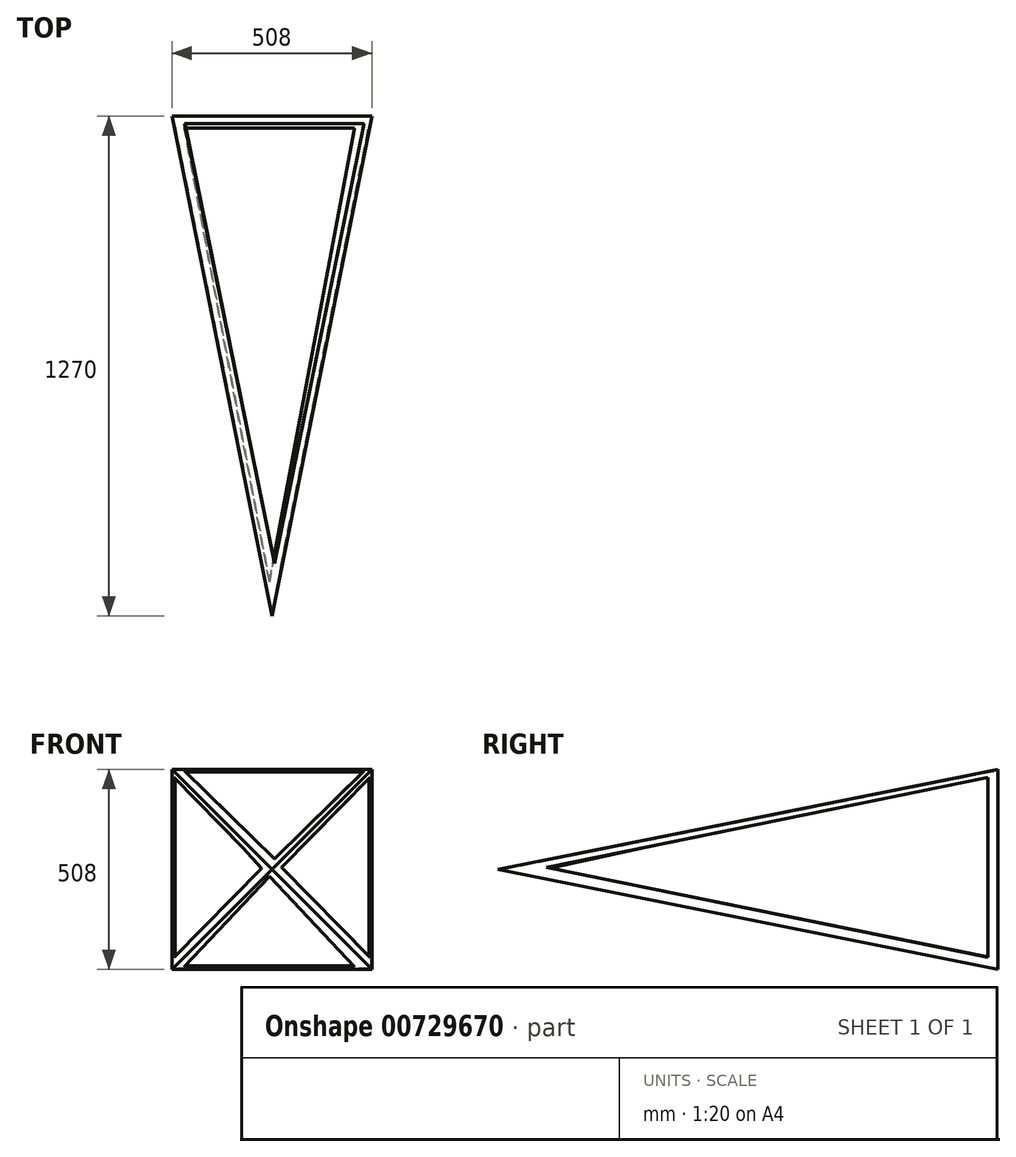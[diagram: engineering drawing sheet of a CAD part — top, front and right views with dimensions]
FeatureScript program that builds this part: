
annotation { "Feature Type Name" : "Feature", "Feature Type Description" : "" }
export const myFeature = defineFeature(function(context is Context, id is Id, definition is map)
    precondition{}
    {
        {
            var Q0;
            Q0=qCreatedBy(makeId("Front.planeOp"),FACE);
            var sketch = newSketch(context, id + "F0", { "sketchPlane" : qUnion([Q0])});
            skLineSegment(sketch, "E0.bottom", {"start": v(0, 0) * mm, "end": v(-508, 0) * mm});
            skLineSegment(sketch, "E0.top", {"start": v(0, 508) * mm, "end": v(-508, 508) * mm});
            skLineSegment(sketch, "E0.left", {"start": v(0, 0) * mm, "end": v(0, 508) * mm});
            skLineSegment(sketch, "E0.right", {"start": v(-508, 0) * mm, "end": v(-508, 508) * mm});
            skSolve(sketch);
        }
        {
            var Q0;
            Q0=makeQuery(id+"F0.imprint","IMPRINT",FACE,{"disambiguationData":[TD([[makeQuery(id+"F0.imprint","IMPRINT",EDGE,{"derivedFrom":sQuery(id+"F0.wireOp",EDGE,"E0.bottom")}),-1.0]])]});
            cPlane(context, id + "F1", {"entities" : qUnion([Q0]), "cplaneType" : CPlaneType.OFFSET, "offset" : 1270 * mm, "width" : 152.4 * mm, "height" : 152.4 * mm});
        }
        {
            var Q0;
            Q0=qCreatedBy(id+"F1.planeOp",FACE);
            var sketch = newSketch(context, id + "F2", { "sketchPlane" : qUnion([Q0])});
            skPoint(sketch, "E1", {"position": v(0, 0) * mm});
            skLineSegment(sketch, "E2.bottom", {"start": v(0, 0) * mm, "end": v(-254, 0) * mm});
            skLineSegment(sketch, "E2.top", {"start": v(0, 254) * mm, "end": v(-254, 254) * mm});
            skLineSegment(sketch, "E2.left", {"start": v(0, 0) * mm, "end": v(0, 254) * mm});
            skLineSegment(sketch, "E2.right", {"start": v(-254, 0) * mm, "end": v(-254, 254) * mm});
            skPoint(sketch, "E3", {"position": v(-254, 254) * mm});
            skSolve(sketch);
        }
        {
            var Q0;
            Q0=makeQuery(id+"F0.imprint","IMPRINT",FACE,{"disambiguationData":[TD([[makeQuery(id+"F0.imprint","IMPRINT",EDGE,{"derivedFrom":sQuery(id+"F0.wireOp",EDGE,"E0.bottom")}),-1.0]])]});
            var Q1;
            Q1=sQuery(id+"F2.wireOp",VERTEX,"E3");
            loft(context, id + "F3", {"sheetProfilesArray" : [{ "sheetProfileEntities" : qUnion([Q0]) }, { "sheetProfileEntities" : qUnion([Q1]) }]});
        }
        {
            var Q0;
            Q0=makeQuery(id+"F3.opLoft","CAP_FACE",FACE,{"disambiguationData":[OSD([makeQuery(id+"F0.imprint","IMPRINT",FACE,{"disambiguationData":[TD([[makeQuery(id+"F0.imprint","IMPRINT",EDGE,{"derivedFrom":sQuery(id+"F0.wireOp",EDGE,"E0.bottom")}),-1.0]])]})])],"isStart":true});
            shell(context, id + "F4", {"entities" : qUnion([Q0]), "thickness" : 2.54 * mm});
        }
        {
            var Q0;
            Q0=makeQuery(id+"F3.opLoft","SWEPT_FACE",FACE,{"disambiguationData":[OSD([sQuery(id+"F0.wireOp",EDGE,"E0.bottom"),sQuery(id+"F0.wireOp",EDGE,"E0.top"),sQuery(id+"F0.wireOp",EDGE,"E0.left")])]});
            cPlane(context, id + "F5", {"entities" : qUnion([Q0]), "cplaneType" : CPlaneType.OFFSET, "offset" : 0 * mm, "width" : 152.4 * mm, "height" : 152.4 * mm});
        }
        {
            var Q0;
            Q0=qCreatedBy(id+"F5.planeOp",FACE);
            var sketch = newSketch(context, id + "F6", { "sketchPlane" : qUnion([Q0])});
            skLineSegment(sketch, "E4", {"start": v(-25.4, 488.34) * mm, "end": v(-25.4, 31.14) * mm});
            skLineSegment(sketch, "E5", {"start": v(-25.4, 31.14) * mm, "end": v(-1168.4, 259.74) * mm});
            skLineSegment(sketch, "E6", {"start": v(-1168.4, 259.74) * mm, "end": v(-25.4, 488.34) * mm});
            skSolve(sketch);
        }
        {
            var Q0;
            Q0 = qSketchRegion(id + "F6", true);
            extrude(context, id + "F7", {"entities" : qUnion([Q0]), "operationType" : NewBodyOperationType.REMOVE, "oppositeDirection" : true, "depth" : 25.4 * mm, "offsetDistance" : 25.4 * mm});
        }
        {
            var Q0;
            Q0=makeQuery(id+"F3.opLoft","SWEPT_FACE",FACE,{"disambiguationData":[OSD([sQuery(id+"F0.wireOp",EDGE,"E0.bottom"),sQuery(id+"F0.wireOp",EDGE,"E0.top"),sQuery(id+"F0.wireOp",EDGE,"E0.right")])]});
            cPlane(context, id + "F8", {"entities" : qUnion([Q0]), "cplaneType" : CPlaneType.OFFSET, "offset" : 0 * mm, "width" : 152.4 * mm, "height" : 152.4 * mm});
        }
        {
            var Q0;
            Q0=qCreatedBy(id+"F8.planeOp",FACE);
            var sketch = newSketch(context, id + "F9", { "sketchPlane" : qUnion([Q0])});
            skLineSegment(sketch, "E7", {"start": v(-73.73, 487.7) * mm, "end": v(-73.73, 30.5) * mm});
            skLineSegment(sketch, "E8", {"start": v(-73.73, 30.5) * mm, "end": v(1069.27, 259.1) * mm});
            skLineSegment(sketch, "E9", {"start": v(1069.27, 259.1) * mm, "end": v(-73.73, 487.7) * mm});
            skLineSegment(sketch, "E10", {"start": v(-100.65, 508) * mm, "end": v(-100.65, 0) * mm});
            skLineSegment(sketch, "E11", {"start": v(-100.65, 508) * mm, "end": v(1115.56, 244.9) * mm});
            skLineSegment(sketch, "E12", {"start": v(1119.53, 244.04) * mm, "end": v(-100.65, 0) * mm});
            skLineSegment(sketch, "E13", {"start": v(-100.65, 254) * mm, "end": v(1169.35, 254) * mm});
            skSolve(sketch);
        }
        {
            var Q0;
            {var subQ3=sQuery(id+"F9.wireOp",EDGE,"E9");var subQ5=sQuery(id+"F9.wireOp",EDGE,"E7");var subQ6=makeQuery(id+"F9.imprint","INTERSECT",VERTEX,{"derivedFrom":[subQ5,subQ3]});Q0=makeQuery(id+"F9.imprint","IMPRINT",FACE,{"disambiguationData":[TD([[makeQuery(id+"F9.imprint","IMPRINT",EDGE,{"disambiguationData":[TD([[subQ6,-1.0]])],"derivedFrom":subQ5}),1.0]])]});}
            var Q1;
            {var subQ0=sQuery(id+"F9.wireOp",EDGE,"E8");var subQ1=sQuery(id+"F9.wireOp",EDGE,"E7");var subQ2=makeQuery(id+"F9.imprint","INTERSECT",VERTEX,{"derivedFrom":[subQ1,subQ0]});Q1=makeQuery(id+"F9.imprint","IMPRINT",FACE,{"disambiguationData":[TD([[makeQuery(id+"F9.imprint","IMPRINT",EDGE,{"disambiguationData":[TD([[subQ2,1.0]])],"derivedFrom":subQ1}),1.0]])]});}
            extrude(context, id + "F10", {"entities" : qUnion([Q0, Q1]), "operationType" : NewBodyOperationType.REMOVE, "oppositeDirection" : true, "depth" : 25.4 * mm, "offsetDistance" : 25.4 * mm});
        }
        {
            var Q0;
            Q0=makeQuery(id+"F3.opLoft","SWEPT_FACE",FACE,{"disambiguationData":[OSD([sQuery(id+"F0.wireOp",EDGE,"E0.top"),sQuery(id+"F0.wireOp",EDGE,"E0.left"),sQuery(id+"F0.wireOp",EDGE,"E0.right")])]});
            cPlane(context, id + "F11", {"entities" : qUnion([Q0]), "cplaneType" : CPlaneType.OFFSET, "offset" : 0 * mm, "width" : 152.4 * mm, "height" : 152.4 * mm});
        }
        {
            var Q0;
            Q0=qCreatedBy(id+"F11.planeOp",FACE);
            var sketch = newSketch(context, id + "F12", { "sketchPlane" : qUnion([Q0])});
            skLineSegment(sketch, "E14", {"start": v(-475.9, 83.78) * mm, "end": v(-18.7, 83.78) * mm});
            skLineSegment(sketch, "E15", {"start": v(-18.7, 83.78) * mm, "end": v(-247.3, -1059.22) * mm});
            skLineSegment(sketch, "E16", {"start": v(-247.3, -1059.22) * mm, "end": v(-475.9, 83.78) * mm});
            skLineSegment(sketch, "E17", {"start": v(0, 80.45) * mm, "end": v(-508, 80.45) * mm});
            skLineSegment(sketch, "E18", {"start": v(-254, 80.45) * mm, "end": v(-254, -1189.55) * mm});
            skSolve(sketch);
        }
        {
            var Q0;
            {var subQ0=sQuery(id+"F12.wireOp",EDGE,"E16");var subQ1=sQuery(id+"F12.wireOp",EDGE,"E15");var subQ2=makeQuery(id+"F12.imprint","INTERSECT",VERTEX,{"derivedFrom":[subQ1,subQ0]});Q0=makeQuery(id+"F12.imprint","IMPRINT",FACE,{"disambiguationData":[TD([[makeQuery(id+"F12.imprint","IMPRINT",EDGE,{"disambiguationData":[TD([[subQ2,1.0]])],"derivedFrom":subQ1}),-1.0]])]});}
            var Q1;
            {var subQ0=sQuery(id+"F12.wireOp",EDGE,"E18");var subQ1=sQuery(id+"F12.wireOp",EDGE,"E16");var subQ2=makeQuery(id+"F12.imprint","INTERSECT",VERTEX,{"derivedFrom":[subQ1,subQ0]});Q1=makeQuery(id+"F12.imprint","IMPRINT",FACE,{"disambiguationData":[TD([[makeQuery(id+"F12.imprint","IMPRINT",EDGE,{"disambiguationData":[TD([[subQ2,-1.0]])],"derivedFrom":subQ1}),-1.0]])]});}
            extrude(context, id + "F13", {"entities" : qUnion([Q0, Q1]), "operationType" : NewBodyOperationType.REMOVE, "oppositeDirection" : true, "depth" : 25.4 * mm, "offsetDistance" : 25.4 * mm});
        }
        {
            var Q0;
            Q0=makeQuery(id+"F3.opLoft","SWEPT_FACE",FACE,{"disambiguationData":[OSD([sQuery(id+"F0.wireOp",EDGE,"E0.bottom"),sQuery(id+"F0.wireOp",EDGE,"E0.left"),sQuery(id+"F0.wireOp",EDGE,"E0.right")])]});
            cPlane(context, id + "F14", {"entities" : qUnion([Q0]), "cplaneType" : CPlaneType.OFFSET, "offset" : 0 * mm, "width" : 152.4 * mm, "height" : 152.4 * mm});
        }
        {
            var Q0;
            Q0=qCreatedBy(id+"F14.planeOp",FACE);
            var sketch = newSketch(context, id + "F15", { "sketchPlane" : qUnion([Q0])});
            skLineSegment(sketch, "E19", {"start": v(-260.36, 1206.67) * mm, "end": v(-476.6, 31.4) * mm});
            skLineSegment(sketch, "E20", {"start": v(-476.6, 31.4) * mm, "end": v(-44.12, 31.4) * mm});
            skLineSegment(sketch, "E21", {"start": v(-44.12, 31.4) * mm, "end": v(-260.36, 1206.67) * mm});
            skSolve(sketch);
        }
        {
            var Q0;
            Q0=makeQuery(id+"F15.imprint","IMPRINT",FACE,{"disambiguationData":[TD([[makeQuery(id+"F15.imprint","IMPRINT",EDGE,{"derivedFrom":sQuery(id+"F15.wireOp",EDGE,"E19")}),1.0]])]});
            extrude(context, id + "F16", {"entities" : qUnion([Q0]), "operationType" : NewBodyOperationType.REMOVE, "oppositeDirection" : true, "depth" : 25.4 * mm, "offsetDistance" : 25.4 * mm});
        }
    });
